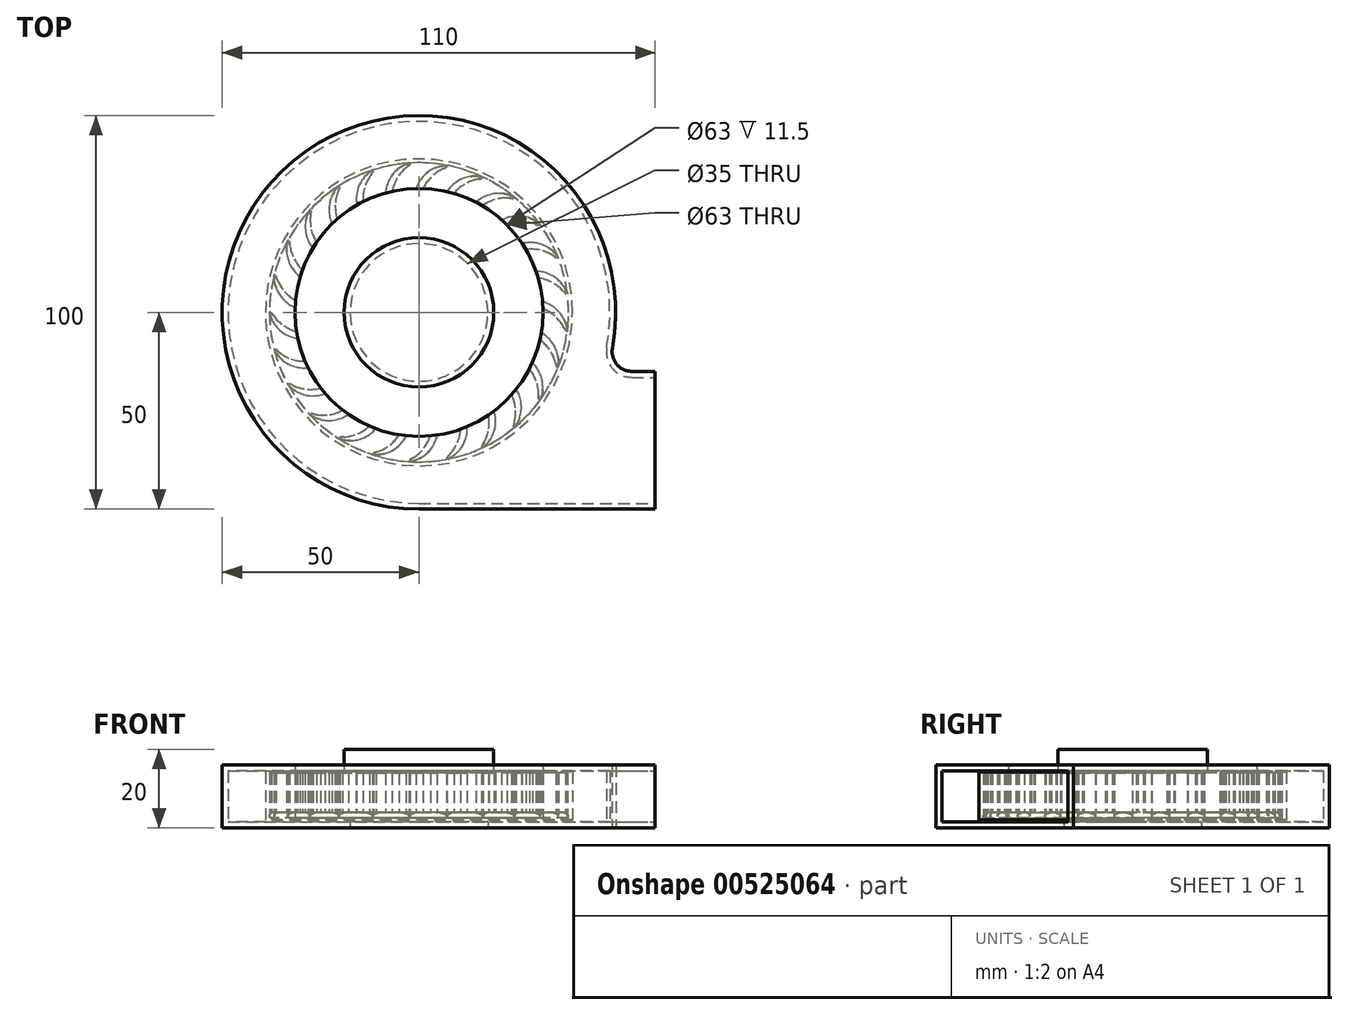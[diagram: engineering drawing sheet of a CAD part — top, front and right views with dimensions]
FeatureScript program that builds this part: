
annotation { "Feature Type Name" : "Feature", "Feature Type Description" : "" }
export const myFeature = defineFeature(function(context is Context, id is Id, definition is map)
    precondition{}
    {
        {
            var Q0;
            Q0=qCreatedBy(makeId("Top.planeOp"),FACE);
            var sketch = newSketch(context, id + "F0", { "sketchPlane" : qUnion([Q0])});
            skCircle(sketch, "E0", {"center": v(0, 0) * mm, "radius": 17.5 * mm});
            skCircle(sketch, "E1", {"center": v(0, 0) * mm, "radius": 38 * mm});
            skLineSegment(sketch, "E2.top", {"start": v(0, -50) * mm, "end": v(60, -50) * mm});
            skLineSegment(sketch, "E3.top", {"start": v(54.08, -15) * mm, "end": v(60, -15) * mm});
            skLineSegment(sketch, "E3.right", {"start": v(60, -50) * mm, "end": v(60, -15) * mm});
            skArc(sketch, "E4", {"start": v(49.17, -9.1) * mm, "mid": v(-31.98, 38.44) * mm, "end": v(0, -50) * mm});
            skCircle(sketch, "E5", {"center": v(0, 0) * mm, "radius": 31.5 * mm});
            skCircle(sketch, "E6", {"center": v(0, 0) * mm, "radius": 25 * mm, "construction": true});
            skPoint(sketch, "E7.visualSharp", {"position": v(47.7, -15) * mm});
            skArc(sketch, "E7.filletArc", {"start": v(49.17, -9.1) * mm, "mid": v(50.24, -13.2) * mm, "end": v(54.08, -15) * mm});
            skSolve(sketch);
        }
        {
            var Q0;
            Q0=qCreatedBy(makeId("Top.planeOp"),FACE);
            var sketch = newSketch(context, id + "F1", { "sketchPlane" : qUnion([Q0])});
            skArc(sketch, "E8", {"start": v(7, 37.1) * mm, "mid": v(1.04, 32.47) * mm, "end": v(0, 25) * mm, "construction": true});
            skArc(sketch, "E9", {"start": v(0.25, 25) * mm, "mid": v(0, 25) * mm, "end": v(-0.25, 25) * mm});
            skArc(sketch, "E10", {"start": v(7.05, 37.34) * mm, "mid": v(0.05, 33.15) * mm, "end": v(-0.25, 25) * mm});
            skArc(sketch, "E11", {"start": v(6.95, 36.85) * mm, "mid": v(1.42, 32.16) * mm, "end": v(0.25, 25) * mm});
            skLineSegment(sketch, "E12", {"start": v(7.05, 37.34) * mm, "end": v(6.95, 36.85) * mm});
            skLineSegment(sketch, "E13", {"start": v(0.05, 33.15) * mm, "end": v(1.42, 32.16) * mm, "construction": true});
            skPoint(sketch, "E14", {"position": v(1.78, 32.47) * mm});
            skPoint(sketch, "E14.positionSnap0", {"position": v(1.04, 32.47) * mm});
            skSolve(sketch);
        }
        {
            var Q0;
            Q0=qCreatedBy(makeId("Front.planeOp"),FACE);
            var sketch = newSketch(context, id + "F2", { "sketchPlane" : qUnion([Q0])});
            skLineSegment(sketch, "E15", {"start": v(0, 34.43) * mm, "end": v(0, -26.28) * mm});
            skSolve(sketch);
        }
        {
            var Q0;
            Q0=makeQuery(id+"F0.imprint","IMPRINT",FACE,{"disambiguationData":[TD([[makeQuery(id+"F0.imprint","IMPRINT",EDGE,{"derivedFrom":sQuery(id+"F0.wireOp",EDGE,"E1")}),1.0]])]});
            var Q1;
            Q1=makeQuery(id+"F0.imprint","IMPRINT",FACE,{"disambiguationData":[TD([[makeQuery(id+"F0.imprint","IMPRINT",EDGE,{"derivedFrom":sQuery(id+"F0.wireOp",EDGE,"E0")}),-1.0]])]});
            var Q2;
            Q2=makeQuery(id+"F0.imprint","IMPRINT",FACE,{"disambiguationData":[TD([[makeQuery(id+"F0.imprint","IMPRINT",EDGE,{"derivedFrom":sQuery(id+"F0.wireOp",EDGE,"E0")}),1.0]])]});
            extrude(context, id + "F3", {"entities" : qUnion([Q0, Q1, Q2]), "oppositeDirection" : true, "depth" : 1.5 * mm});
        }
        {
            var Q0;
            Q0=makeQuery(id+"F0.imprint","IMPRINT",FACE,{"disambiguationData":[TD([[makeQuery(id+"F0.imprint","IMPRINT",EDGE,{"derivedFrom":sQuery(id+"F0.wireOp",EDGE,"E0")}),1.0]])]});
            extrude(context, id + "F4", {"entities" : qUnion([Q0]), "operationType" : NewBodyOperationType.ADD, "depth" : 15 * mm});
        }
        {
            var Q0;
            Q0=makeQuery(id+"F3.opExtrude","CAP_FACE",FACE,{"disambiguationData":[OSD([sQuery(id+"F0.wireOp",EDGE,"E1")])],"isStart":false});
            shell(context, id + "F5", {"entities" : qUnion([Q0]), "thickness" : 1.5 * mm});
        }
        {
            var Q0;
            Q0=makeQuery(id+"F4.opExtrude","CAP_EDGE",EDGE,{"disambiguationData":[OSD([sQuery(id+"F0.wireOp",EDGE,"E0")])],"isStart":false});
            var Q1;
            Q1=makeQuery(id+"F3.opExtrude","CAP_EDGE",EDGE,{"disambiguationData":[OSD([sQuery(id+"F0.wireOp",EDGE,"E1")])],"isStart":true});
            var Q2;
            Q2=makeQuery(id+"F4.opExtrude","CAP_EDGE",EDGE,{"disambiguationData":[OSD([sQuery(id+"F0.wireOp",EDGE,"E0")])],"isStart":true});
            fillet(context, id + "F6", {"entities" : qUnion([Q0, Q1, Q2]), "radius" : 1 * mm, "tangentPropagation" : true, "allowEdgeOverflow" : false});
        }
        {
            var Q0;
            {var subQ0=sQuery(id+"F0.wireOp",EDGE,"E0");Q0=makeQuery(id+"F5.opShell","OFFSET_EDGE",EDGE,{"disambiguationData":[OSD([subQ0]),TDD([makeQuery(id+"F4.opExtrude","CAP_EDGE",EDGE,{"disambiguationData":[OSD([subQ0])],"isStart":true})])]});}
            fillet(context, id + "F7", {"entities" : qUnion([Q0]), "radius" : 2.5 * mm, "tangentPropagation" : true, "allowEdgeOverflow" : false});
        }
        {
            var Q0;
            Q0=qSketchRegion(id+"F1",true);
            extrude(context, id + "F8", {"entities" : qUnion([Q0]), "depth" : 10 * mm, "hasSecondDirection" : true, "secondDirectionOppositeDirection" : true, "secondDirectionDepth" : 1 * mm});
        }
        {
            var Q0;
            Q0=makeQuery(id+"F8.opExtrude","SWEPT_BODY",BODY,{"disambiguationData":[OSD([sQuery(id+"F1.wireOp",EDGE,"E9"),sQuery(id+"F1.wireOp",EDGE,"E10"),sQuery(id+"F1.wireOp",EDGE,"E11"),sQuery(id+"F1.wireOp",EDGE,"E12")])]});
            var Q1;
            Q1=sQuery(id+"F2.wireOp",EDGE,"E15");
            circularPattern(context, id + "F9", {"operationType" : NewBodyOperationType.ADD, "entities" : qUnion([Q0]), "axis" : qUnion([Q1]), "angle" : 360 * degree, "instanceCount" : 25, "equalSpace" : true});
        }
        {
            var Q0;
            Q0=makeQuery(id+"F0.imprint","IMPRINT",FACE,{"disambiguationData":[TD([[makeQuery(id+"F0.imprint","IMPRINT",EDGE,{"derivedFrom":sQuery(id+"F0.wireOp",EDGE,"E1")}),-1.0]])]});
            var Q1;
            Q1=makeQuery(id+"F0.imprint","IMPRINT",FACE,{"disambiguationData":[TD([[makeQuery(id+"F0.imprint","IMPRINT",EDGE,{"derivedFrom":sQuery(id+"F0.wireOp",EDGE,"E0")}),-1.0]])]});
            var Q2;
            Q2=makeQuery(id+"F0.imprint","IMPRINT",FACE,{"disambiguationData":[TD([[makeQuery(id+"F0.imprint","IMPRINT",EDGE,{"derivedFrom":sQuery(id+"F0.wireOp",EDGE,"E1")}),1.0]])]});
            extrude(context, id + "F10", {"entities" : qUnion([Q0, Q1, Q2]), "depth" : 12 * mm, "hasSecondDirection" : true, "secondDirectionOppositeDirection" : true, "secondDirectionDepth" : 4 * mm});
        }
        {
            var Q0;
            Q0=makeQuery(id+"F10.opExtrude","SWEPT_FACE",FACE,{"disambiguationData":[OSD([sQuery(id+"F0.wireOp",EDGE,"E3.right")])]});
            shell(context, id + "F11", {"entities" : qUnion([Q0]), "thickness" : 1.5 * mm});
        }
        {
            var Q0;
            Q0=makeQuery(id+"F0.imprint","IMPRINT",FACE,{"disambiguationData":[TD([[makeQuery(id+"F0.imprint","IMPRINT",EDGE,{"derivedFrom":sQuery(id+"F0.wireOp",EDGE,"E0")}),-1.0]])]});
            var Q1;
            Q1=makeQuery(id+"F0.imprint","IMPRINT",FACE,{"disambiguationData":[TD([[makeQuery(id+"F0.imprint","IMPRINT",EDGE,{"derivedFrom":sQuery(id+"F0.wireOp",EDGE,"E0")}),1.0]])]});
            extrude(context, id + "F12", {"entities" : qUnion([Q0, Q1]), "operationType" : NewBodyOperationType.REMOVE, "depth" : 25 * mm, "hasSecondDirection" : true, "secondDirectionOppositeDirection" : true, "secondDirectionDepth" : 2.5 * mm});
        }
        {
            var Q0;
            Q0=qCreatedBy(makeId("Top.planeOp"),FACE);
            var sketch = newSketch(context, id + "F13", { "sketchPlane" : qUnion([Q0])});
            skCircle(sketch, "E16", {"center": v(0, 0) * mm, "radius": 39 * mm});
            skCircle(sketch, "E17", {"center": v(0, 0) * mm, "radius": 19 * mm});
            skSolve(sketch);
        }
        {
            var Q0;
            Q0=qSketchRegion(id+"F13",true);
            var Q1;
            Q1=makeQuery(id+"F13.imprint","IMPRINT",FACE,{"disambiguationData":[TD([[makeQuery(id+"F13.imprint","IMPRINT",EDGE,{"derivedFrom":sQuery(id+"F13.wireOp",EDGE,"E17")}),1.0]])]});
            extrude(context, id + "F14", {"entities" : qUnion([Q0, Q1]), "depth" : 10.2 * mm, "hasSecondDirection" : true, "secondDirectionOppositeDirection" : true, "secondDirectionDepth" : 2 * mm});
        }
        {
            var Q0;
            Q0=makeQuery(id+"F13.imprint","IMPRINT",FACE,{"disambiguationData":[TD([[makeQuery(id+"F13.imprint","IMPRINT",EDGE,{"derivedFrom":sQuery(id+"F13.wireOp",EDGE,"E17")}),1.0]])]});
            var Q1;
            Q1=sQuery(id+"F13.wireOp",EDGE,"E17");
            extrude(context, id + "F15", {"entities" : qUnion([Q0]), "operationType" : NewBodyOperationType.ADD, "surfaceEntities" : qUnion([Q1]), "depth" : 16 * mm});
        }
    });
